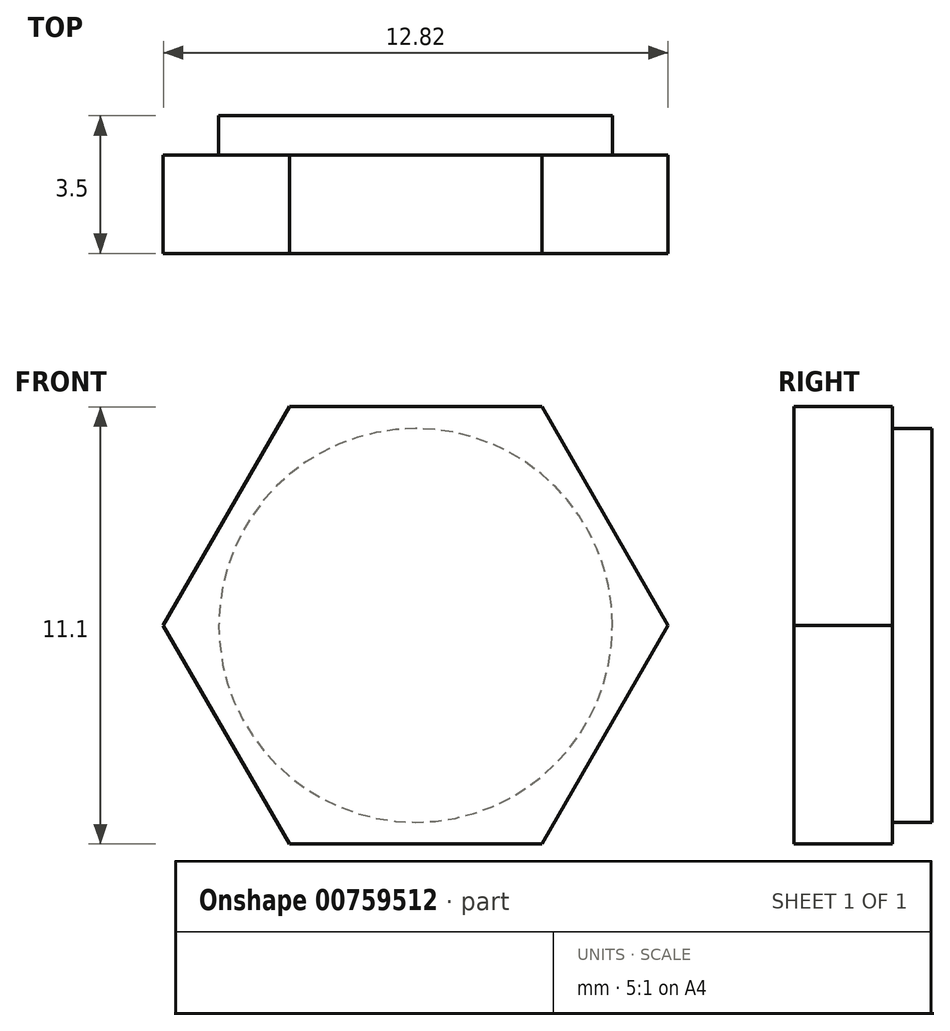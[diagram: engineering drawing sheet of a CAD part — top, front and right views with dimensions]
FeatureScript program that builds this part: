
annotation { "Feature Type Name" : "Feature", "Feature Type Description" : "" }
export const myFeature = defineFeature(function(context is Context, id is Id, definition is map)
    precondition{}
    {
        {
            var Q0;
            Q0=qCreatedBy(makeId("Front.planeOp"),FACE);
            var sketch = newSketch(context, id + "F0", { "sketchPlane" : qUnion([Q0])});
            skCircle(sketch, "E0.cCircle", {"center": v(0, 0) * mm, "radius": 5.56 * mm, "construction": true});
            skLineSegment(sketch, "E0.0", {"start": v(-3.2, 5.56) * mm, "end": v(3.2, 5.56) * mm});
            skLineSegment(sketch, "E0.1", {"start": v(3.2, 5.55) * mm, "end": v(6.41, 0) * mm});
            skLineSegment(sketch, "E0.2", {"start": v(6.41, 0) * mm, "end": v(3.2, -5.56) * mm});
            skLineSegment(sketch, "E0.3", {"start": v(3.2, -5.56) * mm, "end": v(-3.2, -5.56) * mm});
            skLineSegment(sketch, "E0.4", {"start": v(-3.2, -5.56) * mm, "end": v(-6.41, 0) * mm});
            skLineSegment(sketch, "E0.5", {"start": v(-6.41, 0) * mm, "end": v(-3.2, 5.56) * mm});
            skPoint(sketch, "E0.0.midPoint", {"position": v(0, 5.56) * mm});
            skSolve(sketch);
        }
        {
            var Q0;
            Q0 = qSketchRegion(id + "F0", true);
            extrude(context, id + "F1", {"entities" : qUnion([Q0]), "depth" : 2.5 * mm, "offsetDistance" : 25 * mm});
        }
        {
            var Q0;
            Q0=qCreatedBy(makeId("Front.planeOp"),FACE);
            var sketch = newSketch(context, id + "F2", { "sketchPlane" : qUnion([Q0])});
            skCircle(sketch, "E1", {"center": v(0, 0) * mm, "radius": 5 * mm});
            skSolve(sketch);
        }
        {
            var Q0;
            Q0=makeQuery(id+"F2.imprint","IMPRINT",FACE,{"disambiguationData":[TD([[makeQuery(id+"F2.imprint","IMPRINT",EDGE,{"derivedFrom":sQuery(id+"F2.wireOp",EDGE,"E1")}),1.0]])]});
            extrude(context, id + "F3", {"entities" : qUnion([Q0]), "operationType" : NewBodyOperationType.ADD, "oppositeDirection" : true, "depth" : 1 * mm, "offsetDistance" : 25 * mm});
        }
    });
